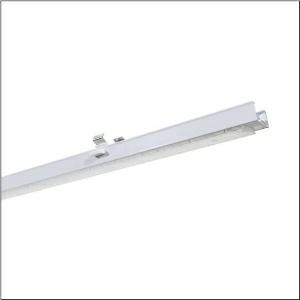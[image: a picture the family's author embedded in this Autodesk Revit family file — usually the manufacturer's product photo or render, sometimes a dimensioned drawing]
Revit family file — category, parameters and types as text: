
# Revit family: trunking_flex_31_51re14mb68b
name_source: partatom
category: Lighting Fixtures
units: mm (PartAtom-declared; Revit-internal decimal feet)

## family parameters
Cut with Voids When Loaded = No
Host = Face
Light Source = No
Part Type = Normal
Room Calculation Point = No
Round Connector Dimension = Use Diameter
Shared = No

## types (1)
- --- (1 x LED, 8000 lm, 50 W, 6500K)
    Apparent Load = 50 VA
    CIE Flux Codes = 72 92 98 99 100
    Color Rendering = 80
    Color Temperature = 6500K
    Default Elevation = 1800 mm
    Description = Trunking Flex 31, luminaire insert, of extruded aluminium section, coated, traffic white (RAL 9016), length: 1.472mm, width: 91mm, height: 53mm, LED rated luminous flux: 8.000lm, light colour: 865, control gear: ON/OFF Multilumen, with system connector: socket, mains connection: 220..240V, AC, 50/60Hz, rated input power: 50W, luminous flux adjustable on luminaire in four steps (4130/5610/6850/8000lm), connected load according to luminous flux setting (25/34/42/50W), primary light control with lens, of plastic, primary optical cover: cover, of PMMA, light emission: direct distribution, primary light characteristic: asymmetric, protection rating (complete): IP20, insulation class (complete): insulation class I (protective earthing), certification: CE, UKCA, impact resistance: IK02, permissible ambient temperature for indoor applications: -20..+40°C, packaging unit: 1 piece
    Height = 58 mm
    Lamp = 1 x LED
    Lamp Light Flux = 8000 lm
    Lamp Power = 50 W
    Lamp count = 1
    Length = 1472 mm
    Luminous efficacy = 160 lm/W
    Manufacturer = Siteco
    ModVariant = No
    Model = 51RE14MB68B
    Mounting Place = Ceiling
    Mounting Type = Pendant
    Number of Poles = 1
    OnlyDefault = Yes
    Power Factor = 1
    Product Name = Trunking Flex 31
    Product group = luminaire insert
    ProductGroupID = 902
    Protection Class = Protection class I
    Protection Degree = IP 20
    RLX_Detail_Level = 1
    RLX_Emergency_Light_Flux = 0 lm
    RLX_Emergency_Type = 0
    RLX_Emergency_Type_DB = No
    RlxData = <blob elided: 21041 chars, md5=cd9c0347>
    Socket = socket
    Standby Power = 0 W
    System Light Flux = 8000 lm
    System Power = 50 W
    Type Comments = factory setting: luminous flux: 100 % | (ON | ON) | 300 mA
    Type Image = l_1266702.jpg
    URL = http://relux.com
    VarID = @adj_059226
    Voltage = 0 V
    Weight = 0.00 kg
    Width = 65 mm

## geometry (parser evidence)
native form markers: Blend x4, Sweep x13
no freeform markers — native parametric forms only
